# Revit family: ВентКлиматСтрой Вентилятор систем дымоудаления осевой ВО-13-284
name_source: partatom
category: Оборудование
units: mm (PartAtom-declared; Revit-internal decimal feet)

## family parameters
Всегда вертикально = Да
Заголовок OmniClass = Fans for Air Ductwork
На основе рабочей плоскости = Нет
Номер OmniClass = 23.75.35.17.11
Общий = Нет
При загрузке вырезать с полостями = Нет
Размер круглого соединителя = Использовать диаметр
Тип детали = Вставляется
Точка расчета площади = Да

## types (22) — shared parameters
ADSK_Версия Revit = 2019
ADSK_Версия семейства = rev.1
ADSK_Единица измерения = шт.
ADSK_Классификация нагрузок = Прочее
ADSK_Количество = 1
ADSK_Количество фаз числовое = 3
ADSK_Коэффициент мощности = 0.8
ADSK_Предел огнестойкости = 120
Poles = 3
zero-valued in all types: ADSK_Материал тип подсчета

## per-type parameters (varying)
| type | D | D1 | D2 | De | L | R1 | Re | d | f | h | l | n | Полюсов | Размер символа УГО |
| ВО 13-284-12К/*-4 4 полюса | 400 мм | 440 мм | 470 мм | 404 мм | 285 мм | 220 мм | 202 мм | 10 мм | 30 мм | 255 мм | 283 мм | 8 | 4 | 0.4 |
| ВО 13-284-12К/*-4 2 полюса | 400 мм | 440 мм | 470 мм | 404 мм | 285 мм | 220 мм | 202 мм | 10 мм | 30 мм | 255 мм | 283 мм | 8 | 2 | 0.4 |
| ВО 13-284-12К/*-4,5 4 полюса | 450 мм | 490 мм | 520 мм | 454 мм | 285 мм | 245 мм | 227 мм | 10 мм | 30 мм | 280 мм | 283 мм | 8 | 4 | 0.4 |
| ВО 13-284-12К/*-4,5 2 полюса | 450 мм | 490 мм | 520 мм | 454 мм | 285 мм | 245 мм | 227 мм | 10 мм | 30 мм | 280 мм | 283 мм | 8 | 2 | 0.4 |
| ВО 13-284-12К/*-5 4 полюса | 500 мм | 540 мм | 570 мм | 504 мм | 385 мм | 270 мм | 252 мм | 10 мм | 30 мм | 305 мм | 383 мм | 12 | 4 | 0.4 |
| ВО 13-284-12К/*-5 2 полюса | 500 мм | 540 мм | 570 мм | 504 мм | 385 мм | 270 мм | 252 мм | 10 мм | 30 мм | 305 мм | 383 мм | 12 | 2 | 0.4 |
| ВО 13-284-12К/*-5,6 4 полюса | 560 мм | 600 мм | 630 мм | 564 мм | 385 мм | 300 мм | 282 мм | 10 мм | 35 мм | 335 мм | 383 мм | 12 | 4 | 0.4 |
| ВО 13-284-12К/*-5,6 2 полюса | 560 мм | 600 мм | 630 мм | 564 мм | 385 мм | 300 мм | 282 мм | 10 мм | 35 мм | 335 мм | 383 мм | 12 | 2 | 0.4 |
| ВО 13-284-12К/*-6,3 4 полюса | 630 мм | 670 мм | 700 мм | 634 мм | 485 мм | 335 мм | 317 мм | 10 мм | 35 мм | 370 мм | 483 мм | 12 | 4 | 0.4 |
| ВО 13-284-12К/*-6,3 2 полюса | 630 мм | 670 мм | 700 мм | 634 мм | 485 мм | 335 мм | 317 мм | 10 мм | 35 мм | 370 мм | 483 мм | 12 | 2 | 0.4 |
| ВО 13-284-12К/*-7,1 6 полюсов | 710 мм | 750 мм | 790 мм | 714 мм | 485 мм | 375 мм | 357 мм | 10 мм | 35 мм | 410 мм | 483 мм | 16 | 6 | 0.4 |
| ВО 13-284-12К/*-7,1 4 полюса | 710 мм | 750 мм | 790 мм | 714 мм | 485 мм | 375 мм | 357 мм | 10 мм | 35 мм | 410 мм | 483 мм | 16 | 4 | 0.4 |
| ВО 13-284-12К/*-8 6 полюсов | 800 мм | 840 мм | 880 мм | 804 мм | 485 мм | 420 мм | 402 мм | 10 мм | 35 мм | 455 мм | 483 мм | 16 | 6 | 0.4 |
| ВО 13-284-12К/*-8 4 полюса | 800 мм | 840 мм | 880 мм | 804 мм | 485 мм | 420 мм | 402 мм | 10 мм | 35 мм | 455 мм | 483 мм | 16 | 4 | 0.4 |
| ВО 13-284-12К/*-9 6 полюсов | 900 мм | 950 мм | 990 мм | 904 мм | 485 мм | 475 мм | 452 мм | 10 мм | 40 мм | 505 мм | 483 мм | 16 | 6 | 0.388889 |
| ВО 13-284-12К/*-9 4 полюса | 900 мм | 950 мм | 990 мм | 904 мм | 485 мм | 475 мм | 452 мм | 10 мм | 40 мм | 505 мм | 483 мм | 16 | 4 | 0.388889 |
| ВО 13-284-12К/*-10 6 полюсов | 1000 мм | 1050 мм | 1090 мм | 1004 мм | 485 мм | 525 мм | 502 мм | 10 мм | 40 мм | 555 мм | 483 мм | 16 | 6 | 0.335 |
| ВО 13-284-12К/*-10 4 полюса | 1000 мм | 1050 мм | 1090 мм | 1004 мм | 485 мм | 525 мм | 502 мм | 10 мм | 40 мм | 555 мм | 483 мм | 16 | 4 | 0.335 |
| ВО 13-284-12К/*-11,2 6 полюсов | 1120 мм | 1170 мм | 1210 мм | 1124 мм | 615 мм | 585 мм | 562 мм | 12 мм | 50 мм | 625 мм | 613 мм | 20 | 6 | 0.399107 |
| ВО 13-284-12К/*-11,2 4 полюса | 1120 мм | 1170 мм | 1210 мм | 1124 мм | 615 мм | 585 мм | 562 мм | 12 мм | 50 мм | 625 мм | 613 мм | 20 | 4 | 0.399107 |
| ВО 13-284-12К/*-12,5 8 полюсов | 1250 мм | 1300 мм | 1340 мм | 1254 мм | 615 мм | 650 мм | 627 мм | 12 мм | 50 мм | 700 мм | 613 мм | 20 | 8 | 0.342 |
| ВО 13-284-12К/*-12,5 6 полюсов | 1250 мм | 1300 мм | 1340 мм | 1254 мм | 615 мм | 650 мм | 627 мм | 12 мм | 50 мм | 700 мм | 613 мм | 20 | 6 | 0.342 |

## geometry (parser evidence)
native form markers: Sweep x3
no freeform markers — native parametric forms only
